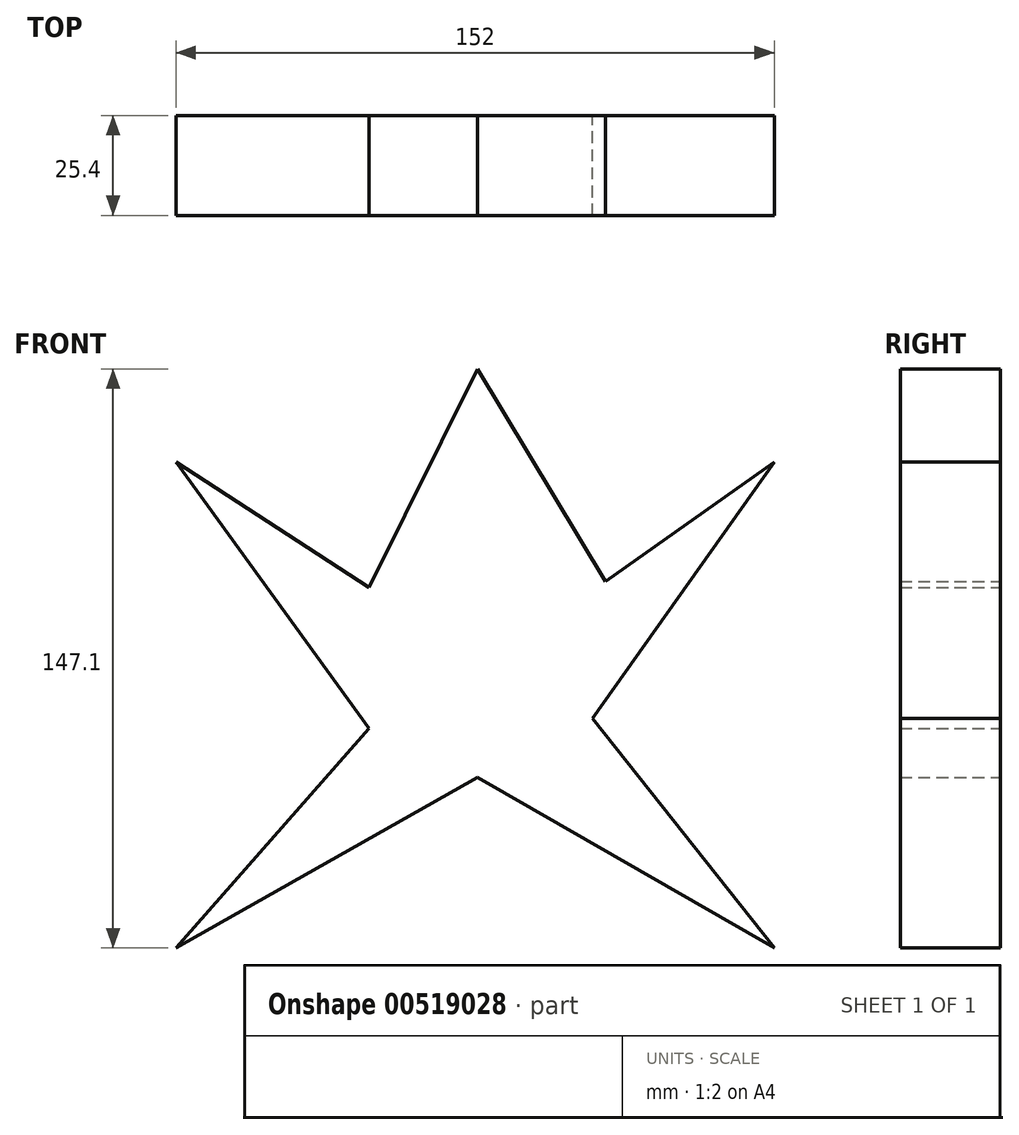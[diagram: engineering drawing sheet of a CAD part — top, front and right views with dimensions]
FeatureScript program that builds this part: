
annotation { "Feature Type Name" : "Feature", "Feature Type Description" : "" }
export const myFeature = defineFeature(function(context is Context, id is Id, definition is map)
    precondition{}
    {
        {
            var Q0;
            Q0=qCreatedBy(makeId("Front.planeOp"),FACE);
            var sketch = newSketch(context, id + "F0", { "sketchPlane" : qUnion([Q0])});
            skLineSegment(sketch, "E0", {"start": v(-27.59, 16.1) * mm, "end": v(0, 71.57) * mm});
            skLineSegment(sketch, "E1", {"start": v(0, 71.57) * mm, "end": v(32.5, 17.54) * mm});
            skLineSegment(sketch, "E2", {"start": v(32.5, 17.54) * mm, "end": v(75.42, 47.97) * mm});
            skLineSegment(sketch, "E3", {"start": v(75.42, 47.97) * mm, "end": v(29.27, -17.17) * mm});
            skLineSegment(sketch, "E4", {"start": v(-27.59, 16.1) * mm, "end": v(-76.58, 47.97) * mm});
            skLineSegment(sketch, "E5", {"start": v(-76.58, 47.97) * mm, "end": v(-27.59, -19.7) * mm});
            skLineSegment(sketch, "E6", {"start": v(-27.59, -19.7) * mm, "end": v(-76.58, -75.53) * mm});
            skLineSegment(sketch, "E7", {"start": v(-76.58, -75.53) * mm, "end": v(0, -32.2) * mm});
            skLineSegment(sketch, "E8", {"start": v(29.27, -17.17) * mm, "end": v(75.42, -75.53) * mm});
            skLineSegment(sketch, "E9", {"start": v(75.42, -75.53) * mm, "end": v(0, -32.2) * mm});
            skSolve(sketch);
        }
        {
            var Q0;
            Q0=makeQuery(id+"F0.imprint","IMPRINT",FACE,{"disambiguationData":[TD([[makeQuery(id+"F0.imprint","IMPRINT",EDGE,{"derivedFrom":sQuery(id+"F0.wireOp",EDGE,"E0")}),-1.0]])]});
            extrude(context, id + "F1", {"entities" : qUnion([Q0]), "endBound" : BoundingType.SYMMETRIC, "depth" : 25.4 * mm, "offsetDistance" : 25.4 * mm});
        }
    });
